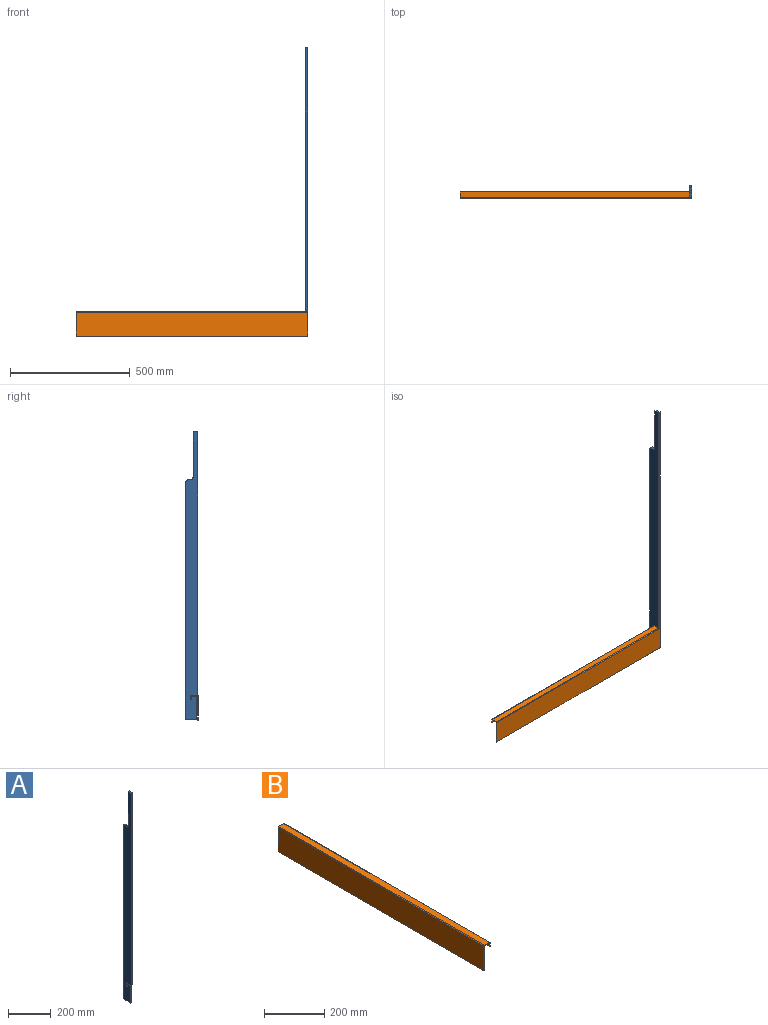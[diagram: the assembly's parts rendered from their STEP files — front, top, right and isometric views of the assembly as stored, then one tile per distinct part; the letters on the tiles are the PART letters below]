
ASSEMBLY  parts=2 mates=1
PART A: 16 faces, bbox 10x50x1200 mm
  f0: plane 1098x10mm, normal (0,-1,0), area 10980mm2, adj f2,f3,f9,f10
  f1: plane 46x10mm, normal (0,0,-1), area 460mm2, adj f2,f3,f4,f11
  f2: plane 1200x50mm, normal (1,0,0), area 53427.5mm2, adj f0,f1,f4,f5,f6,f7,f8,f9
  f3: plane 1200x50mm, normal (-1,0,0), area 53427.5mm2, adj f0,f1,f4,f5,f6,f7,f8,f9
  f4: plane 990x10mm, normal (0,1,0), area 9900mm2, adj f1,f2,f3,f5
  f5: cylinder r=10mm len=10mm, axis (-1,0,0), area 157.1mm2, adj f2,f3,f4,f6
  f6: plane 10x10mm, normal (0,0,1), area 100mm2, adj f2,f3,f5,f7
  f7: cylinder r=10mm len=10mm, axis (-1,0,0), area 157.1mm2, adj f2,f3,f6,f8
  f8: plane 190x10mm, normal (0,1,0), area 1900mm2, adj f2,f3,f7,f9
  f9: plane 20x10mm, normal (0,0,1), area 200mm2, adj f0,f2,f3,f8
  f10: plane 30x10mm, normal (0,0,-1), area 300mm2, adj f0,f2,f3,f15
  f11: plane 98x10mm, normal (0,-1,0), area 980mm2, adj f1,f2,f3,f12
  f12: plane 22x10mm, normal (0,0,1), area 220mm2, adj f2,f3,f11,f13
  f13: plane 15.13x10mm, normal (0,1,0), area 151.3mm2, adj f2,f3,f12,f14
  f14: plane 10x4mm, normal (0,0,1), area 40mm2, adj f2,f3,f13,f15
  f15: plane 19.13x10mm, normal (0,-1,0), area 191.3mm2, adj f2,f3,f10,f14
PART B: 22 faces, bbox 29.2x965x101.6 mm
  f0: plane 24x1.6mm, normal (0,1,0), area 38.4mm2, adj f2,f3,f10,f19
  f1: plane 24x1.6mm, normal (0,-1,0), area 38.4mm2, adj f2,f3,f9,f18
  f2: plane 965x24mm, normal (0,0,1), area 23160mm2, adj f0,f1,f11,f20
  f3: plane 965x24mm, normal (0,0,-1), area 23160mm2, adj f0,f1,f12,f21
  f4: plane 15x1.6mm, normal (0,1,0), area 24mm2, adj f6,f7,f8,f10
  f5: plane 15x1.6mm, normal (0,-1,0), area 24mm2, adj f6,f7,f8,f9
  f6: plane 965x1.6mm, normal (0,0,-1), area 1544mm2, adj f4,f5,f7,f8
  f7: plane 965x15mm, normal (1,0,0), area 14475mm2, adj f4,f5,f6,f11
  f8: plane 965x15mm, normal (-1,0,0), area 14475mm2, adj f4,f5,f6,f12
  f9: plane 2.6x2.6mm, normal (0,-1,0), area 4.5mm2, adj f1,f5,f11,f12
  f10: plane 2.6x2.6mm, normal (0,1,0), area 4.5mm2, adj f0,f4,f11,f12
  f11: cylinder r=2.6mm len=965mm, axis (0,-1,0), area 3941.1mm2, adj f2,f7,f9,f10
  f12: cylinder r=1mm len=965mm, axis (0,-1,0), area 1515.8mm2, adj f3,f8,f9,f10
  f13: plane 99x1.6mm, normal (0,1,0), area 158.4mm2, adj f14,f16,f17,f19
  f14: plane 965x1.6mm, normal (0,0,-1), area 1544mm2, adj f13,f15,f16,f17
  f15: plane 99x1.6mm, normal (0,-1,0), area 158.4mm2, adj f14,f16,f17,f18
  f16: plane 965x99mm, normal (-1,0,0), area 95535mm2, adj f13,f14,f15,f20
  f17: plane 965x99mm, normal (1,0,0), area 95535mm2, adj f13,f14,f15,f21
  f18: plane 2.6x2.6mm, normal (0,-1,0), area 4.5mm2, adj f1,f15,f20,f21
  f19: plane 2.6x2.6mm, normal (0,1,0), area 4.5mm2, adj f0,f13,f20,f21
  f20: cylinder r=2.6mm len=965mm, axis (0,-1,0), area 3941.1mm2, adj f2,f16,f18,f19
  f21: cylinder r=1mm len=965mm, axis (0,-1,0), area 1515.8mm2, adj f3,f17,f18,f19
PLACE A t=(-285.02,61.79,-71.37)mm
PLACE B rot(axis=(0,0,1),90deg) t=(-1240.02,59.11,-215.85)mm
MATE fastened B.f8 <-> A.f13  axis (0,-1,0) through (-275.02,67.79,-174.44)mm
